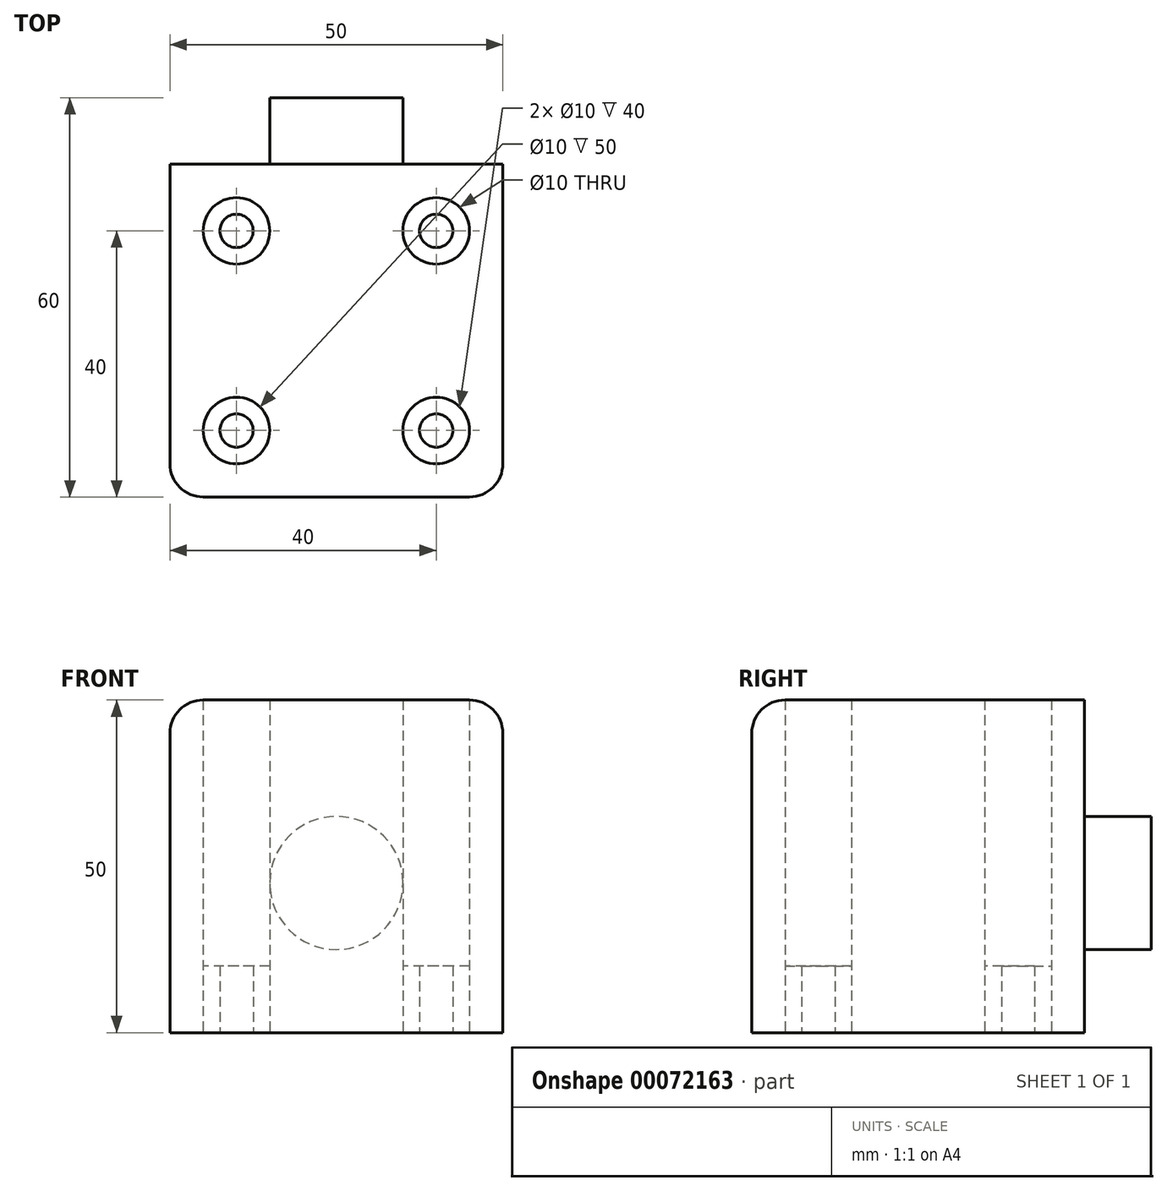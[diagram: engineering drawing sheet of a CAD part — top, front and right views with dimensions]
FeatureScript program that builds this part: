
annotation { "Feature Type Name" : "Feature", "Feature Type Description" : "" }
export const myFeature = defineFeature(function(context is Context, id is Id, definition is map)
    precondition{}
    {
        {
            var Q0;
            Q0=qCreatedBy(makeId("Top.planeOp"),FACE);
            var sketch = newSketch(context, id + "F0", { "sketchPlane" : qUnion([Q0])});
            skLineSegment(sketch, "E0.bottom", {"start": v(-25, 25) * mm, "end": v(25, 25) * mm});
            skLineSegment(sketch, "E0.top", {"start": v(-25, -25) * mm, "end": v(25, -25) * mm});
            skLineSegment(sketch, "E0.left", {"start": v(-25, 25) * mm, "end": v(-25, -25) * mm});
            skLineSegment(sketch, "E0.right", {"start": v(25, 25) * mm, "end": v(25, -25) * mm});
            skCircle(sketch, "E1", {"center": v(-15, 15) * mm, "radius": 5 * mm});
            skCircle(sketch, "E2", {"center": v(-15, 15) * mm, "radius": 2.5 * mm});
            skLineSegment(sketch, "E3", {"start": v(-33.92, 33.92) * mm, "end": v(33.92, -33.92) * mm, "construction": true});
            skLineSegment(sketch, "E4", {"start": v(-32.97, -32.97) * mm, "end": v(32.97, 32.97) * mm, "construction": true});
            skLineSegment(sketch, "E5", {"start": v(-36.07, 0) * mm, "end": v(34.94, 0) * mm, "construction": true});
            skPoint(sketch, "E5.endSnap0", {"position": v(-25, 0) * mm});
            skLineSegment(sketch, "E6", {"start": v(0, 32.26) * mm, "end": v(0, -36.39) * mm, "construction": true});
            skCircle(sketch, "E7.MirrorC", {"center": v(-15, -15) * mm, "radius": 2.5 * mm});
            skCircle(sketch, "E8.MirrorC", {"center": v(-15, -15) * mm, "radius": 5 * mm});
            skCircle(sketch, "E9.MirrorC", {"center": v(15, -15) * mm, "radius": 5 * mm});
            skCircle(sketch, "E10.MirrorC", {"center": v(15, -15) * mm, "radius": 2.5 * mm});
            skCircle(sketch, "E11.MirrorC", {"center": v(15, 15) * mm, "radius": 2.5 * mm});
            skCircle(sketch, "E12.MirrorC", {"center": v(15, 15) * mm, "radius": 5 * mm});
            skSolve(sketch);
        }
        {
            var Q0;
            Q0=makeQuery(id+"F0.imprint","IMPRINT",FACE,{"disambiguationData":[TD([[makeQuery(id+"F0.imprint","IMPRINT",EDGE,{"derivedFrom":sQuery(id+"F0.wireOp",EDGE,"E0.bottom")}),-1.0]])]});
            var Q1;
            Q1=makeQuery(id+"F0.imprint","IMPRINT",FACE,{"disambiguationData":[TD([[makeQuery(id+"F0.imprint","IMPRINT",EDGE,{"derivedFrom":sQuery(id+"F0.wireOp",EDGE,"E7.MirrorC")}),1.0]])]});
            var Q2;
            Q2=makeQuery(id+"F0.imprint","IMPRINT",FACE,{"disambiguationData":[TD([[makeQuery(id+"F0.imprint","IMPRINT",EDGE,{"derivedFrom":sQuery(id+"F0.wireOp",EDGE,"E1")}),1.0]])]});
            var Q3;
            Q3=makeQuery(id+"F0.imprint","IMPRINT",FACE,{"disambiguationData":[TD([[makeQuery(id+"F0.imprint","IMPRINT",EDGE,{"derivedFrom":sQuery(id+"F0.wireOp",EDGE,"E11.MirrorC")}),1.0]])]});
            var Q4;
            Q4=makeQuery(id+"F0.imprint","IMPRINT",FACE,{"disambiguationData":[TD([[makeQuery(id+"F0.imprint","IMPRINT",EDGE,{"derivedFrom":sQuery(id+"F0.wireOp",EDGE,"E9.MirrorC")}),1.0]])]});
            extrude(context, id + "F1", {"entities" : qUnion([Q0, Q1, Q2, Q3, Q4]), "depth" : 50 * mm});
        }
        {
            var Q0;
            Q0=makeQuery(id+"F0.imprint","IMPRINT",FACE,{"disambiguationData":[TD([[makeQuery(id+"F0.imprint","IMPRINT",EDGE,{"derivedFrom":sQuery(id+"F0.wireOp",EDGE,"E7.MirrorC")}),1.0]])]});
            var Q1;
            Q1=makeQuery(id+"F0.imprint","IMPRINT",FACE,{"disambiguationData":[TD([[makeQuery(id+"F0.imprint","IMPRINT",EDGE,{"derivedFrom":sQuery(id+"F0.wireOp",EDGE,"E1")}),1.0]])]});
            var Q2;
            Q2=makeQuery(id+"F0.imprint","IMPRINT",FACE,{"disambiguationData":[TD([[makeQuery(id+"F0.imprint","IMPRINT",EDGE,{"derivedFrom":sQuery(id+"F0.wireOp",EDGE,"E9.MirrorC")}),1.0]])]});
            var Q3;
            Q3=makeQuery(id+"F0.imprint","IMPRINT",FACE,{"disambiguationData":[TD([[makeQuery(id+"F0.imprint","IMPRINT",EDGE,{"derivedFrom":sQuery(id+"F0.wireOp",EDGE,"E11.MirrorC")}),1.0]])]});
            var Q4;
            Q4=makeQuery(id+"F1.opExtrude","CAP_FACE",FACE,{"disambiguationData":[OSD([sQuery(id+"F0.wireOp",EDGE,"E0.bottom"),sQuery(id+"F0.wireOp",EDGE,"E0.top"),sQuery(id+"F0.wireOp",EDGE,"E0.left"),sQuery(id+"F0.wireOp",EDGE,"E0.right"),sQuery(id+"F0.wireOp",EDGE,"E2"),sQuery(id+"F0.wireOp",EDGE,"E7.MirrorC"),sQuery(id+"F0.wireOp",EDGE,"E10.MirrorC"),sQuery(id+"F0.wireOp",EDGE,"E11.MirrorC")])],"isStart":false});
            extrude(context, id + "F2", {"entities" : qUnion([Q0, Q1, Q2, Q3]), "operationType" : NewBodyOperationType.REMOVE, "endBound" : BoundingType.UP_TO_SURFACE, "endBoundEntityFace" : qUnion([Q4]), "depth" : 25 * mm, "hasSecondDirection" : true, "secondDirectionOppositeDirection" : false, "secondDirectionDepth" : 10 * mm});
        }
        {
            var Q0;
            Q0=makeQuery(id+"F1.opExtrude","SWEPT_EDGE",EDGE,{"disambiguationData":[OSD([sQuery(id+"F0.wireOp",EDGE,"E0.top"),sQuery(id+"F0.wireOp",EDGE,"E0.left")])]});
            var Q1;
            Q1=makeQuery(id+"F1.opExtrude","SWEPT_EDGE",EDGE,{"disambiguationData":[OSD([sQuery(id+"F0.wireOp",EDGE,"E0.top"),sQuery(id+"F0.wireOp",EDGE,"E0.right")])]});
            var Q2;
            Q2=makeQuery(id+"F1.opExtrude","CAP_EDGE",EDGE,{"disambiguationData":[OSD([sQuery(id+"F0.wireOp",EDGE,"E0.top")])],"isStart":false});
            var Q3;
            Q3=makeQuery(id+"F1.opExtrude","CAP_EDGE",EDGE,{"disambiguationData":[OSD([sQuery(id+"F0.wireOp",EDGE,"E0.left")])],"isStart":false});
            var Q4;
            Q4=makeQuery(id+"F1.opExtrude","CAP_EDGE",EDGE,{"disambiguationData":[OSD([sQuery(id+"F0.wireOp",EDGE,"E0.right")])],"isStart":false});
            fillet(context, id + "F3", {"entities" : qUnion([Q0, Q1, Q2, Q3, Q4]), "radius" : 5 * mm, "tangentPropagation" : true, "allowEdgeOverflow" : false});
        }
        {
            var Q0;
            Q0=makeQuery(id+"F1.opExtrude","SWEPT_FACE",FACE,{"disambiguationData":[OSD([sQuery(id+"F0.wireOp",EDGE,"E0.bottom")])]});
            var sketch = newSketch(context, id + "F4", { "sketchPlane" : qUnion([Q0])});
            skCircle(sketch, "E13", {"center": v(0, 22.5) * mm, "radius": 10 * mm});
            skPoint(sketch, "E13.centerSnap0", {"position": v(0, 0) * mm});
            skPoint(sketch, "E13.centerSnap1", {"position": v(-25, 22.5) * mm});
            skSolve(sketch);
        }
        {
            var Q0;
            Q0=makeQuery(id+"F4.imprint","IMPRINT",FACE,{"disambiguationData":[TD([[makeQuery(id+"F4.imprint","IMPRINT",EDGE,{"derivedFrom":sQuery(id+"F4.wireOp",EDGE,"E13")}),1.0]])]});
            extrude(context, id + "F5", {"entities" : qUnion([Q0]), "operationType" : NewBodyOperationType.ADD, "depth" : 10 * mm});
        }
    });
